# Revit family: v-624_6047k(l)8_k9(-bk)(-bl)_50Hz
name_source: partatom
category: 機械設備
units: mm (PartAtom-declared; Revit-internal decimal feet)

## family parameters
OmniClass タイトル = Centrifugal Fans
OmniClass 番号 = 23.75.35.17.27
パーツ タイプ = 標準
ロード時にボイドで切り取り = いいえ
丸型コネクタ寸法 = 直径を使用
作業面ベース = いいえ
共有 = いいえ
常に垂直 = はい
部屋計算ポイント = いいえ

## types (16) — shared parameters
D3 = 55  [stored 0.180446 ft]
Duct_D = 145  [stored 0.475722 ft]
Duct_Height = 55  [stored 0.180446 ft]
EAサイズ_D = 148  [stored 0.485564 ft]
H1 = 129  [stored 0.423228 ft]
Height = 400  [stored 1.31234 ft]
IfcExportAs = IfcFanType
IfcExportType = CENTRIFUGALFORWARDCURVED
MAX静圧 = 0.0 Pa
MID静圧 = 0.0 Pa
MIN静圧 = 0.0 Pa
OmniClassCode = 23-33 31 19 13 15
URL = https://www.mitsubishielectric.co.jp
Uniclass2015Code = Pr_65_67_29_12
Uniclass2015Title = Centrifugal fans
Uniclass2015Version = Systems v1.9
☑給気／□排気 = いいえ
ダクト径 = 150 mm
仕様書バージョン = Version1.0
企業コード = 108420
分類コード = 50052503100060
周波数 = 50 Hz
呼称 = 遠心送風機
外気量 = 0.0 m³/h
天吊用穴_D_右・左配管 = 290  [stored 0.951444 ft]
天吊用穴_D_後・上配管 = 255  [stored 0.836614 ft]
天吊用穴_ピッチ = 480  [stored 1.5748 ft]
実風量 = 0.0 m³/h
形式 = 片吸込形
排気量 = 0.0 m³/h
極数 = 2
機外静圧 = 0.0 Pa
機外静圧_排気 = 210.0 Pa
法定耐用年数 = 15
相 = 1
積算_科目 = 2 換気設備
符号 = FE
製品リリース年月 = 2022年6月1日
製品出荷対象 = 国内
製造元 = 三菱電機株式会社
設置方法 = 天吊
設計風量 = 0.0 m³/h
説明 = レンジフードファン 深形 標準タイプ
負荷分類 = 3_ファン類
運転質量 = 0.00 kg
電動機出力 = 0 W
電圧 = 100 V
zero-valued in all types: Clearance Back, Clearance Bottom, Clearance Front, Clearance Left, Clearance Right, Clearance Top

## per-type parameters (varying)
| type | D1 | D2 | Depth | H2 | MAX風量 | MID風量 | MIN風量 | W1 | Width | マテリアル | 価格 | 消費電力 | 製品質量 | 質量 | 風量 | 騒音レベル(dB(A)) |
| V-602K9 | 419 | 400  [stored 1.31234 ft] | 600  [stored 1.9685 ft] | 600  [stored 1.9685 ft] | 445.0 m³/h | 0.0 m³/h | 295.0 m³/h | 300  [stored 0.984252 ft] | 600  [stored 1.9685 ft] | 鋼板(白) | 88200 $ | 50 W | 14.50 kg | 17.40 kg | 445.0 m³/h | 36 |
| V-602K9-BK | 419 | 400  [stored 1.31234 ft] | 600  [stored 1.9685 ft] | 600  [stored 1.9685 ft] | 445.0 m³/h | 0.0 m³/h | 295.0 m³/h | 300  [stored 0.984252 ft] | 600  [stored 1.9685 ft] | 鋼板(黒) | 88200 $ | 50 W | 14.50 kg | 17.40 kg | 445.0 m³/h | 36 |
| V-604K9 | 419 | 400  [stored 1.31234 ft] | 600  [stored 1.9685 ft] | 600  [stored 1.9685 ft] | 600.0 m³/h | 350.0 m³/h | 230.0 m³/h | 300  [stored 0.984252 ft] | 600  [stored 1.9685 ft] | 鋼板(白) | 108100 $ | 77 W | 16.50 kg | 19.80 kg | 600.0 m³/h | 39.5 |
| V-604K9-BK | 419 | 400  [stored 1.31234 ft] | 600  [stored 1.9685 ft] | 600  [stored 1.9685 ft] | 600.0 m³/h | 350.0 m³/h | 230.0 m³/h | 300  [stored 0.984252 ft] | 600  [stored 1.9685 ft] | 鋼板(黒) | 108100 $ | 77 W | 16.50 kg | 19.80 kg | 600.0 m³/h | 39.5 |
| V-605K9 | 419 | 400  [stored 1.31234 ft] | 600  [stored 1.9685 ft] | 600  [stored 1.9685 ft] | 785.0 m³/h | 460.0 m³/h | 325.0 m³/h | 300  [stored 0.984252 ft] | 600  [stored 1.9685 ft] | 鋼板(白) | 119200 $ | 132 W | 16.50 kg | 19.80 kg | 785.0 m³/h | 45.5 |
| V-605K9-BK | 419 | 400  [stored 1.31234 ft] | 600  [stored 1.9685 ft] | 600  [stored 1.9685 ft] | 785.0 m³/h | 460.0 m³/h | 325.0 m³/h | 300  [stored 0.984252 ft] | 600  [stored 1.9685 ft] | 鋼板(黒) | 119200 $ | 132 W | 16.50 kg | 19.80 kg | 785.0 m³/h | 45.5 |
| V-754K9 | 419 | 400  [stored 1.31234 ft] | 600  [stored 1.9685 ft] | 600  [stored 1.9685 ft] | 600.0 m³/h | 350.0 m³/h | 230.0 m³/h | 375  [stored 1.23031 ft] | 750  [stored 2.46063 ft] | 鋼板(白) | 144700 $ | 77 W | 18.50 kg | 22.20 kg | 600.0 m³/h | 39.5 |
| V-603K8-BL | 469 | 375  [stored 1.23031 ft] | 650  [stored 2.13255 ft] | 600  [stored 1.9685 ft] | 580.0 m³/h | 345.0 m³/h | 200.0 m³/h | 300  [stored 0.984252 ft] | 600  [stored 1.9685 ft] | 鋼板(白) | 100700 $ | 72 W | 17.00 kg | 20.40 kg | 580.0 m³/h | 38.5 |
| V-604K8-BL | 469 | 375  [stored 1.23031 ft] | 650  [stored 2.13255 ft] | 600  [stored 1.9685 ft] | 660.0 m³/h | 380.0 m³/h | 255.0 m³/h | 300  [stored 0.984252 ft] | 600  [stored 1.9685 ft] | 鋼板(白) | 103500 $ | 118 W | 17.00 kg | 20.40 kg | 660.0 m³/h | 43 |
| V-603KL8-BL | 469 | 375  [stored 1.23031 ft] | 650  [stored 2.13255 ft] | 600  [stored 1.9685 ft] | 580.0 m³/h | 345.0 m³/h | 200.0 m³/h | 300  [stored 0.984252 ft] | 600  [stored 1.9685 ft] | 鋼板(白) | 103500 $ | 72 W | 17.00 kg | 20.40 kg | 580.0 m³/h | 38.5 |
| V-604KL8-BL | 469 | 375  [stored 1.23031 ft] | 650  [stored 2.13255 ft] | 600  [stored 1.9685 ft] | 660.0 m³/h | 380.0 m³/h | 255.0 m³/h | 300  [stored 0.984252 ft] | 600  [stored 1.9685 ft] | 鋼板(白) | 106500 $ | 118 W | 17.00 kg | 20.40 kg | 660.0 m³/h | 43 |
| V-6037K8-BL | 469 | 375  [stored 1.23031 ft] | 650  [stored 2.13255 ft] | 700  [stored 2.29659 ft] | 580.0 m³/h | 345.0 m³/h | 200.0 m³/h | 300  [stored 0.984252 ft] | 600  [stored 1.9685 ft] | 鋼板(白) | 105100 $ | 72 W | 17.50 kg | 21.00 kg | 580.0 m³/h | 38.5 |
| V-6037KL8-BL | 469 | 375  [stored 1.23031 ft] | 650  [stored 2.13255 ft] | 700  [stored 2.29659 ft] | 580.0 m³/h | 345.0 m³/h | 200.0 m³/h | 300  [stored 0.984252 ft] | 600  [stored 1.9685 ft] | 鋼板(白) | 107900 $ | 72 W | 17.50 kg | 21.00 kg | 580.0 m³/h | 38.5 |
| V-6047K8-BL | 469 | 375  [stored 1.23031 ft] | 650  [stored 2.13255 ft] | 700  [stored 2.29659 ft] | 660.0 m³/h | 380.0 m³/h | 255.0 m³/h | 300  [stored 0.984252 ft] | 600  [stored 1.9685 ft] | 鋼板(白) | 107900 $ | 118 W | 17.50 kg | 21.00 kg | 660.0 m³/h | 43 |
| V-6047KL8-BL | 469 | 375  [stored 1.23031 ft] | 650  [stored 2.13255 ft] | 700  [stored 2.29659 ft] | 660.0 m³/h | 380.0 m³/h | 255.0 m³/h | 300  [stored 0.984252 ft] | 600  [stored 1.9685 ft] | 鋼板(白) | 110800 $ | 118 W | 17.50 kg | 21.00 kg | 660.0 m³/h | 43 |
| V-6027KL8-BL | 469 | 375  [stored 1.23031 ft] | 650  [stored 2.13255 ft] | 700  [stored 2.29659 ft] | 480.0 m³/h | 310.0 m³/h | 200.0 m³/h | 300  [stored 0.984252 ft] | 600  [stored 1.9685 ft] | 鋼板(白) | 107900 $ | 67 W | 17.50 kg | 21.00 kg | 480.0 m³/h | 38 |

note: column(s) folded — value = type name in every type: モデル

note: [stored X ft] marks values corroborated as IEEE doubles in the binary element streams (Revit-internal decimal feet)
